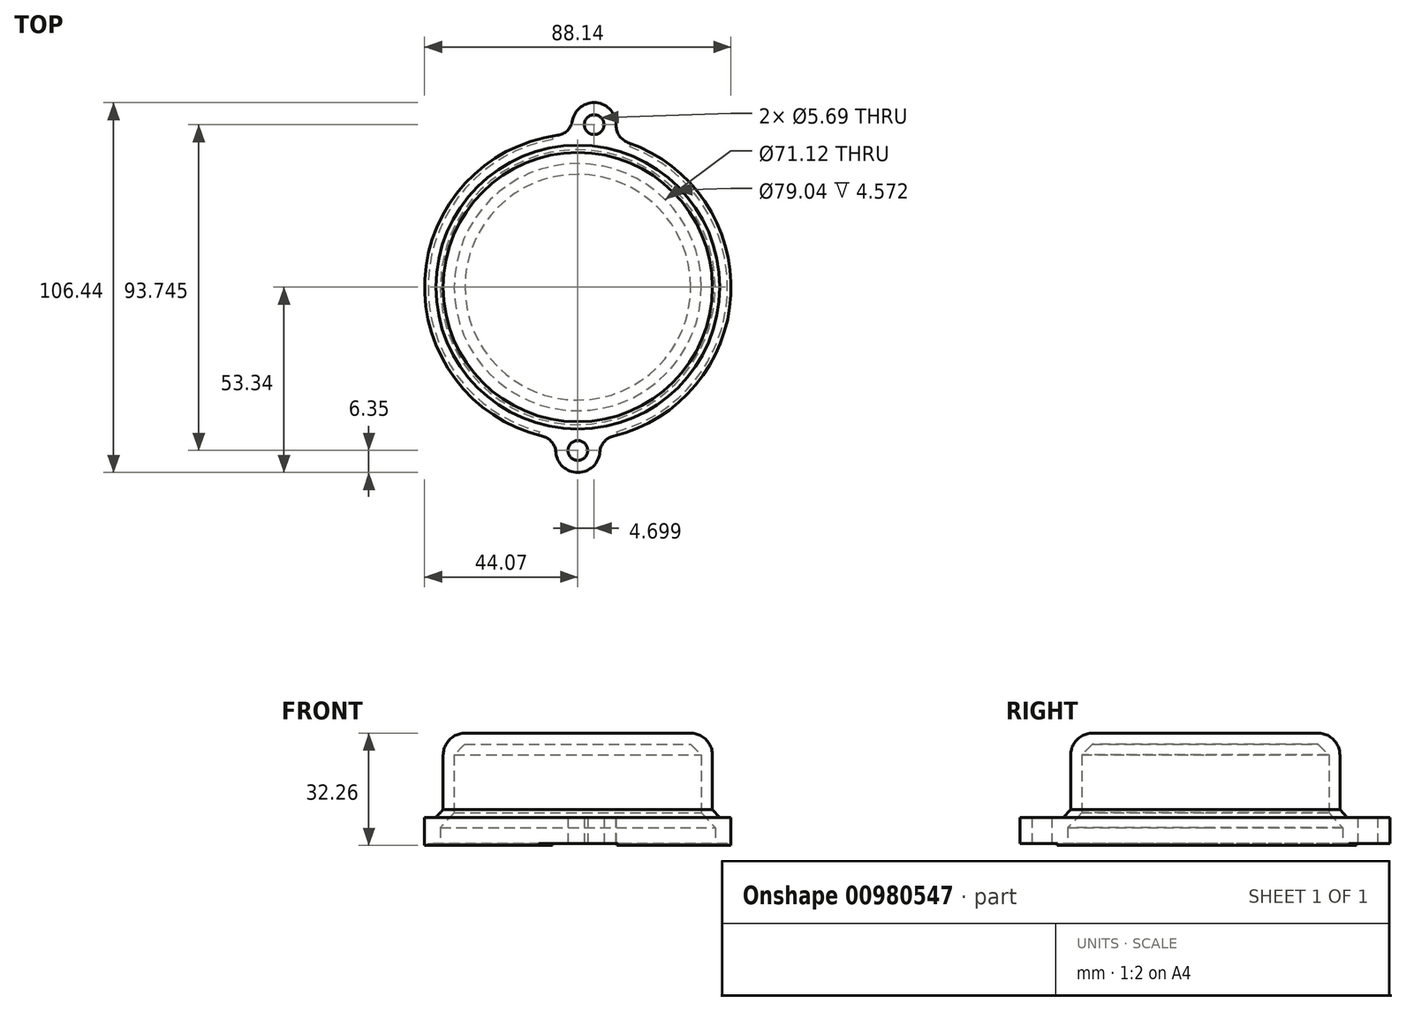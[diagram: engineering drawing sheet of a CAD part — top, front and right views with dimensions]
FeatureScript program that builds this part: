
annotation { "Feature Type Name" : "Feature", "Feature Type Description" : "" }
export const myFeature = defineFeature(function(context is Context, id is Id, definition is map)
    precondition{}
    {
        {
            var Q0;
            Q0=qCreatedBy(makeId("Front.planeOp"),FACE);
            var sketch = newSketch(context, id + "F0", { "sketchPlane" : qUnion([Q0])});
            skLineSegment(sketch, "E0", {"start": v(0, 31.75) * mm, "end": v(32.38, 31.75) * mm});
            skLineSegment(sketch, "E1", {"start": v(0, 28.58) * mm, "end": v(0, 31.75) * mm});
            skLineSegment(sketch, "E2", {"start": v(35.56, 25.5) * mm, "end": v(35.56, 8.83) * mm});
            skLineSegment(sketch, "E3", {"start": v(39.52, 0) * mm, "end": v(43.05, 0) * mm});
            skLineSegment(sketch, "E4", {"start": v(43.05, 0) * mm, "end": v(43.05, -0.5) * mm});
            skLineSegment(sketch, "E5", {"start": v(43.05, -0.5) * mm, "end": v(44.07, -0.5) * mm});
            skLineSegment(sketch, "E6", {"start": v(44.07, -0.5) * mm, "end": v(44.07, 7.52) * mm});
            skLineSegment(sketch, "E7", {"start": v(40.83, 7.52) * mm, "end": v(44.07, 7.52) * mm});
            skLineSegment(sketch, "E8", {"start": v(38.73, 25.4) * mm, "end": v(38.73, 9.77) * mm});
            skLineSegment(sketch, "E9", {"start": v(0, 28.58) * mm, "end": v(32.49, 28.58) * mm});
            skPoint(sketch, "E10.visualSharp", {"position": v(38.73, 31.75) * mm});
            skArc(sketch, "E10.filletArc", {"start": v(38.74, 25.4) * mm, "mid": v(36.88, 29.9) * mm, "end": v(32.38, 31.75) * mm});
            skLineSegment(sketch, "E11", {"start": v(32.49, 28.58) * mm, "end": v(35.56, 25.5) * mm});
            skLineSegment(sketch, "E12", {"start": v(39.52, 0) * mm, "end": v(39.52, 4.57) * mm});
            skLineSegment(sketch, "E13", {"start": v(39.52, 4.57) * mm, "end": v(35.56, 8.83) * mm});
            skLineSegment(sketch, "E14", {"start": v(38.73, 9.77) * mm, "end": v(40.83, 7.52) * mm});
            skSolve(sketch);
        }
        {
            var Q0;
            Q0 = qSketchRegion(id + "F0", true);
            var Q1;
            Q1=sQuery(id+"F0.wireOp",EDGE,"E1");
            revolve(context, id + "F1", {"surfaceOperationType" : NewSurfaceOperationType.NEW, "entities" : qUnion([Q0]), "axis" : qUnion([Q1]), "revolveType" : RevolveType.FULL});
        }
        {
            var Q0;
            Q0=makeQuery(id+"F1.opRevolve","SWEPT_FACE",FACE,{"disambiguationData":[OSD([sQuery(id+"F0.wireOp",EDGE,"E3")])]});
            var sketch = newSketch(context, id + "F2", { "sketchPlane" : qUnion([Q0])});
            skCircle(sketch, "E15", {"center": v(0, 47) * mm, "radius": 2.84 * mm});
            skCircle(sketch, "E16", {"center": v(0, 47) * mm, "radius": 6.35 * mm});
            skCircle(sketch, "E17", {"center": v(4.7, -46.75) * mm, "radius": 2.84 * mm});
            skCircle(sketch, "E18", {"center": v(4.7, -46.75) * mm, "radius": 6.35 * mm});
            skSolve(sketch);
        }
        {
            var Q0;
            Q0=makeQuery(id+"F2.imprint","IMPRINT",FACE,{"disambiguationData":[TD([[makeQuery(id+"F2.imprint","IMPRINT",EDGE,{"derivedFrom":sQuery(id+"F2.wireOp",EDGE,"E15")}),-1.0]])]});
            extrude(context, id + "F3", {"entities" : qUnion([Q0]), "operationType" : NewBodyOperationType.ADD, "depth" : -7.52 * mm, "offsetDistance" : 25.4 * mm});
        }
        {
            var Q0;
            Q0 = qSketchRegion(id + "F2", true);
            extrude(context, id + "F4", {"entities" : qUnion([Q0]), "operationType" : NewBodyOperationType.ADD, "depth" : -7.52 * mm, "offsetDistance" : 25.4 * mm});
        }
        {
            var Q0;
            Q0=makeQuery(id+"F4.boolean.opBoolean","INTERSECT",EDGE,{"disambiguationData":[OD(0.0)],"derivedFrom":[makeQuery(id+"F1.opRevolve","SWEPT_FACE",FACE,{"disambiguationData":[OSD([sQuery(id+"F0.wireOp",EDGE,"E6")])]}),makeQuery(id+"F4.opExtrude","SWEPT_FACE",FACE,{"disambiguationData":[OSD([sQuery(id+"F2.wireOp",EDGE,"E18")])]})]});
            fillet(context, id + "F5", {"entities" : qUnion([Q0]), "radius" : 5.08 * mm, "tangentPropagation" : true, "allowEdgeOverflow" : false});
        }
        {
            var Q0;
            Q0=makeQuery(id+"F3.boolean.opBoolean","INTERSECT",EDGE,{"disambiguationData":[OD(0.0)],"derivedFrom":[makeQuery(id+"F1.opRevolve","SWEPT_FACE",FACE,{"disambiguationData":[OSD([sQuery(id+"F0.wireOp",EDGE,"E6")])]}),makeQuery(id+"F3.opExtrude","SWEPT_FACE",FACE,{"disambiguationData":[OSD([sQuery(id+"F2.wireOp",EDGE,"E16")])]})]});
            fillet(context, id + "F6", {"entities" : qUnion([Q0]), "radius" : 5.08 * mm, "tangentPropagation" : true, "allowEdgeOverflow" : false});
        }
        {
            var Q0;
            Q0=makeQuery(id+"F3.boolean.opBoolean","INTERSECT",EDGE,{"disambiguationData":[OD(1.0)],"derivedFrom":[makeQuery(id+"F1.opRevolve","SWEPT_FACE",FACE,{"disambiguationData":[OSD([sQuery(id+"F0.wireOp",EDGE,"E6")])]}),makeQuery(id+"F3.opExtrude","SWEPT_FACE",FACE,{"disambiguationData":[OSD([sQuery(id+"F2.wireOp",EDGE,"E16")])]})]});
            var Q1;
            Q1=makeQuery(id+"F4.boolean.opBoolean","INTERSECT",EDGE,{"disambiguationData":[OD(1.0)],"derivedFrom":[makeQuery(id+"F1.opRevolve","SWEPT_FACE",FACE,{"disambiguationData":[OSD([sQuery(id+"F0.wireOp",EDGE,"E6")])]}),makeQuery(id+"F4.opExtrude","SWEPT_FACE",FACE,{"disambiguationData":[OSD([sQuery(id+"F2.wireOp",EDGE,"E18")])]})]});
            fillet(context, id + "F7", {"entities" : qUnion([Q0, Q1]), "radius" : 5.08 * mm, "tangentPropagation" : true, "allowEdgeOverflow" : false});
        }
        {
            var Q0;
            Q0=makeQuery(id+"F2.imprint","IMPRINT",FACE,{"disambiguationData":[TD([[makeQuery(id+"F2.imprint","IMPRINT",EDGE,{"derivedFrom":sQuery(id+"F2.wireOp",EDGE,"E15")}),-1.0]])]});
            var sketch = newSketch(context, id + "F8", { "sketchPlane" : qUnion([Q0])});
            skArc(sketch, "E19", {"start": v(11.55, 42.6) * mm, "mid": v(0.12, 44.13) * mm, "end": v(-11.31, 42.66) * mm});
            skArc(sketch, "E20", {"start": v(11.22, 41.52) * mm, "mid": v(0.15, 43) * mm, "end": v(-10.94, 41.6) * mm});
            skLineSegment(sketch, "E21", {"start": v(-11.31, 42.66) * mm, "end": v(-10.94, 41.6) * mm});
            skLineSegment(sketch, "E22", {"start": v(11.55, 42.6) * mm, "end": v(11.22, 41.52) * mm});
            skArc(sketch, "E23", {"start": v(-7.42, -43.51) * mm, "mid": v(4.1, -43.96) * mm, "end": v(15.33, -41.34) * mm});
            skArc(sketch, "E24", {"start": v(-7.24, -42.32) * mm, "mid": v(3.94, -42.76) * mm, "end": v(14.85, -40.28) * mm});
            skLineSegment(sketch, "E25", {"start": v(-7.42, -43.51) * mm, "end": v(-7.24, -42.32) * mm});
            skLineSegment(sketch, "E26", {"start": v(15.33, -41.34) * mm, "end": v(14.85, -40.28) * mm});
            skSolve(sketch);
        }
        {
            var Q0;
            Q0 = qSketchRegion(id + "F8", true);
            extrude(context, id + "F9", {"entities" : qUnion([Q0]), "operationType" : NewBodyOperationType.REMOVE, "oppositeDirection" : true, "depth" : -0.5 * mm, "offsetDistance" : 25.4 * mm});
        }
    });
